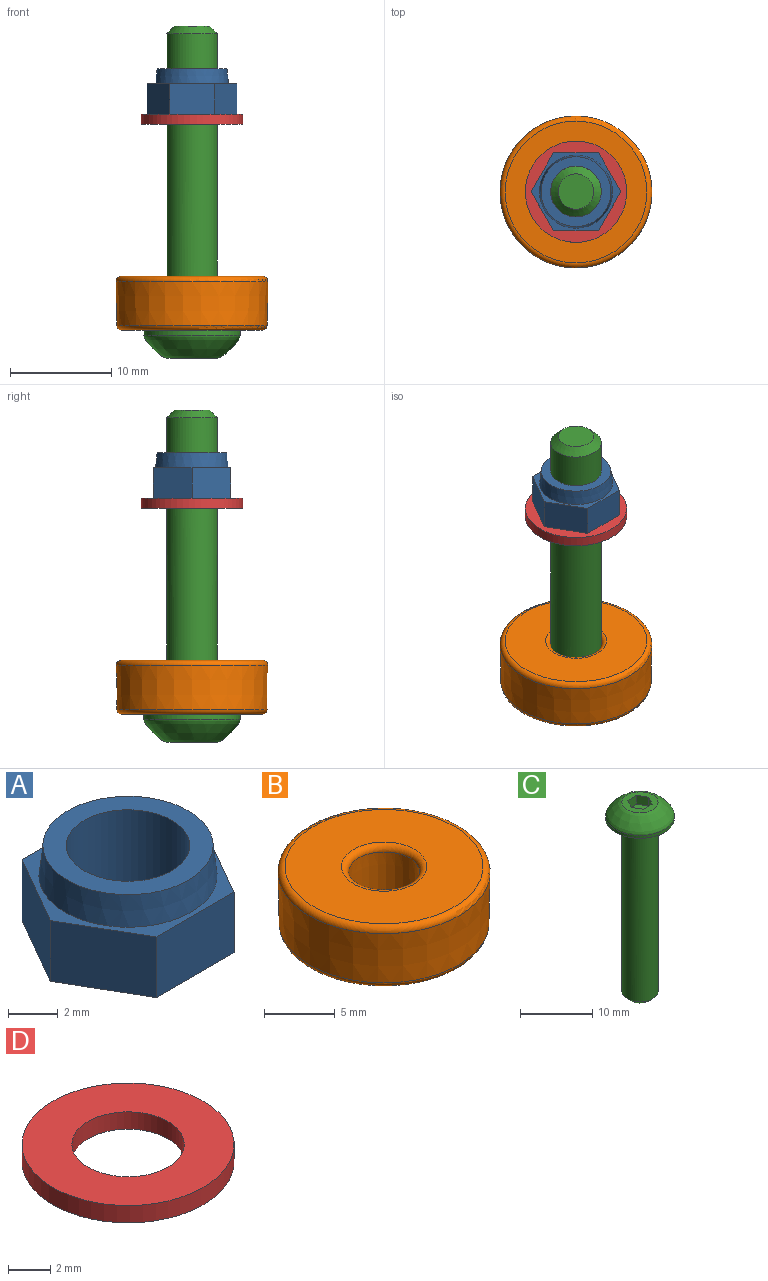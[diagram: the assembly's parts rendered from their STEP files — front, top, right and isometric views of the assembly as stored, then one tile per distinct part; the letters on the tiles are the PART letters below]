
ASSEMBLY  parts=4 mates=3
PART A: 11 faces, bbox 8.9x7.7x4.5 mm
  f0: plane 3.84x3mm, normal (-0.87,0.5,0), area 13.3mm2, adj f1,f5,f6,f7
  f1: plane 3.84x3mm, normal (-0.87,-0.5,0), area 13.3mm2, adj f0,f2,f6,f7
  f2: plane 4.43x3mm, normal (0,-1,0), area 13.3mm2, adj f1,f3,f6,f7
  f3: plane 3.84x3mm, normal (0.87,-0.5,0), area 13.3mm2, adj f2,f4,f6,f7
  f4: plane 3.84x3mm, normal (0.87,0.5,0), area 13.3mm2, adj f3,f5,f6,f7
  f5: plane 4.43x3mm, normal (0,1,0), area 13.3mm2, adj f0,f4,f6,f7
  f6: plane 8.87x7.68mm, normal (0,0,1), area 10.4mm2, adj f0,f1,f2,f3,f4,f5,f8
  f7: plane 8.87x7.68mm, normal (0,0,-1), area 31.4mm2, adj f0,f1,f2,f3,f4,f5,f10
  f8: cone r=3.6mm half-angle=6deg, axis (0,0,-1), area 33.4mm2, adj f6,f9
  f9: plane 6.88x6.88mm, normal (0,0,1), area 17.6mm2, adj f8,f10
  f10: cylinder r=2.5mm len=5mm, axis (0,0,1), area 70.7mm2, adj f7,f9
PART B: 8 faces, bbox 16.2x16.2x5.3 mm
  f0: cone r=2.5mm half-angle=1deg, axis (0,0,-1), area 68.8mm2, adj f4,f6
  f1: cone r=7.5mm half-angle=1deg, axis (0,0,1), area 201.4mm2, adj f5,f7
  f2: plane 13.83x13.83mm, normal (0,0,-1), area 120.4mm2, adj f6,f7
  f3: plane 13.98x13.98mm, normal (0,0,1), area 125.1mm2, adj f4,f5
  f4: torus R=3.01mm, axis (0,0,1), area 13.4mm2, adj f0,f3
  f5: torus R=6.99mm, axis (0,0,1), area 36.5mm2, adj f1,f3
  f6: torus R=3.08mm, axis (0,0,1), area 13.5mm2, adj f0,f2
  f7: torus R=6.92mm, axis (0,0,1), area 35.3mm2, adj f1,f2
PART C: 14 faces, bbox 9.5x9.5x32.8 mm
  f0: plane 5.01x5.01mm, normal (0,0,1), area 11.8mm2, adj f3,f4,f5,f6,f7,f8,f10
  f1: cylinder r=4.75mm len=9.5mm, axis (0,0,-1), area 14.9mm2, adj f2,f10
  f2: plane 9.5x9.5mm, normal (0,0,-1), area 51.2mm2, adj f1,f11
  f3: plane 1.5x1.5mm, normal (-0.87,-0.5,0), area 2.6mm2, adj f0,f4,f8,f9
  f4: plane 1.73x1.5mm, normal (0,-1,0), area 2.6mm2, adj f0,f3,f5,f9
  f5: plane 1.5x1.5mm, normal (0.87,-0.5,0), area 2.6mm2, adj f0,f4,f6,f9
  f6: plane 1.5x1.5mm, normal (0.87,0.5,0), area 2.6mm2, adj f0,f5,f7,f9
  f7: plane 1.73x1.5mm, normal (0,1,0), area 2.6mm2, adj f0,f6,f8,f9
  f8: plane 1.5x1.5mm, normal (-0.87,0.5,0), area 2.6mm2, adj f0,f3,f7,f9
  f9: plane 3.46x3mm, normal (0,0,1), area 7.8mm2, adj f3,f4,f5,f6,f7,f8
  f10: bspline ~9.5x9.5mm, area 78.3mm2, adj f0,f1
  f11: cylinder r=2.5mm len=29.25mm, axis (0,0,1), area 459.5mm2, adj f2,f13
  f12: plane 3.5x3.5mm, normal (0,0,-1), area 9.6mm2, adj f13
  f13: cone r=1.75mm half-angle=45deg, axis (0,0,1), area 14.2mm2, adj f11,f12
PART D: 4 faces, bbox 10x10x1 mm
  f0: cylinder r=2.65mm len=5.3mm, axis (0,0,-1), area 16.7mm2, adj f2,f3
  f1: cylinder r=5mm len=10mm, axis (0,0,-1), area 31.4mm2, adj f2,f3
  f2: plane 10x10mm, normal (0,0,1), area 56.5mm2, adj f0,f1
  f3: plane 10x10mm, normal (0,0,-1), area 56.5mm2, adj f0,f1
PLACE A t=(-13.81,-6.82,11.96)mm
PLACE B t=(-13.81,-6.82,-4.04)mm
PLACE C rot(axis=(1,0,0),180deg) t=(48.69,-6.82,-9.34)mm
PLACE D t=(-13.81,-6.82,10.96)mm
MATE fastened B.f0 <-> D.f0  axis (0,0,1) through (-13.81,-6.82,-4.04)mm
MATE fastened D.f0 <-> A.f8  axis (0,0,1) through (-13.81,-6.82,11.96)mm
MATE fastened C.f1 <-> B.f0  axis (0,0,1) through (-13.81,-6.82,-9.34)mm
